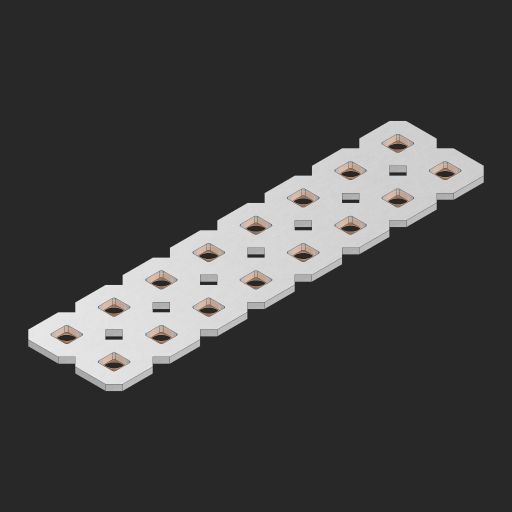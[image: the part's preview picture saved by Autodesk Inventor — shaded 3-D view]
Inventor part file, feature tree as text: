
AUTODESK INVENTOR PART (.ipt)
format: ipt  version: 2023 (Build 270158000, 158)  size: 465,920 bytes
history: native  units: in
note: dims shown in document units (in); Inventor stores cm internally (conversion verified against a paired STEP export)
features: other x17, extrude x15, sketch x2, pattern_linear x1
ambient origin geometry x8: Origin, YZ Plane, XZ Plane, XY Plane, X Axis, Y Axis, Z Axis, Center Point
bodies: Solid1 (feature_tree), Body (feature_tree)
feature tree (35):
  pattern_linear  "Rectangular Pattern1"  Spacing1=0.09in  [1 undecoded]
  sketch  "Sketch1"  dims[d1=0.5in]
  sketch  "Sketch2"  dims[d2=0.182in d3=0.09in d4=0.09in d5=0.09in d6=0.09in d7=0.09in d8=0.09in d9=0.09in d10=0.09in d11=0.02in d13=0.0in d14=0.172in d15=0.0625in d16=0.0in d19=0.5in d22=0.5in]
  other  "Srf1"
  other  "Srf126"
  other  "Srf127"
  other  "Srf128"
  other  "Srf129"
  other  "Srf130"
  other  "Srf131"
  other  "Srf250"
  other  "Srf268"
  other  "Srf269"
  other  "Srf270"
  other  "Srf271"
  other  "Srf272"
  other  "Srf273"
  other  "Srf274"
  other  "Srf275"
  other  "Circle"
  extrude  "ExtrusionSrf126"  Depth=0.09in
  extrude  "ExtrusionSrf127"  Depth=0.09in
  extrude  "ExtrusionSrf128"  Depth=0.09in
  extrude  "ExtrusionSrf129"  Depth=0.09in
  extrude  "ExtrusionSrf130"  Depth=0.09in
  extrude  "ExtrusionSrf131"  Depth=0.09in
  extrude  "ExtrusionSrf250"  Depth=0.09in
  extrude  "ExtrusionSrf268"  Depth=0.02in
  extrude  "ExtrusionSrf269"  TaperAngle=0.0deg  [1 undecoded]
  extrude  "ExtrusionSrf270"  Depth=0.5in
  extrude  "ExtrusionSrf271"  Depth=0.0625in TaperAngle=0.0deg
  extrude  "ExtrusionSrf272"  Depth=0.5in
  extrude  "ExtrusionSrf273"  Depth=0.5in
  extrude  "ExtrusionSrf274"  [1 undecoded]
  extrude  "ExtrusionSrf275"  [1 undecoded]
note: 4 required parameter values undecoded (feature->parameter linkage not recoverable at this tier; creation-order binding heuristic only, values carry confidence <= 0.55)
